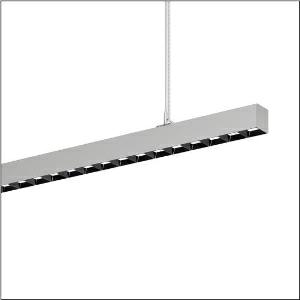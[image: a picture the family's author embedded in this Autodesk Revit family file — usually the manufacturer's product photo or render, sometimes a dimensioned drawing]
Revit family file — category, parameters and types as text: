
# Revit family: silica_r__21_51mx32tat7s_c957
name_source: partatom
category: Lighting Fixtures
units: mm (PartAtom-declared; Revit-internal decimal feet)

## family parameters
Cut with Voids When Loaded = No
Host = Face
Light Source = No
Part Type = Normal
Room Calculation Point = No
Round Connector Dimension = Use Diameter
Shared = No

## types (1)
- --- (1 x LED, 6220 lm, 53.4 W, 6500K)
    Apparent Load = 53 VA
    CIE Flux Codes = 84 99 100 60 100
    Color Rendering = 80
    Color Temperature = 6500K
    Default Elevation = 1800 mm
    Description = Silica® 21, office luminaire, primary light control with darklight reflector, of PMMA, black, CAT 2 (L<= 3000cd/m²), light emission: direct/indirect distribution, primary light characteristic: symmetric, installation type: suspended mounting, LED, rated luminous flux: 6.220lm, luminous efficacy: 111lm/W, light colour: 8tw, colour temperature: 2700..6500K, control gear: ECG DALI, with terminal, 3+2-pole, max. 2.5mm², mains connection: 220..240V, AC, 50/60Hz, rated input power: 56.1W, luminaire housing, of aluminium, metallic grey (RAL 9006), length: 1.204mm, width: 53mm, height: 53mm, protection rating (complete): IP20, insulation class (complete): insulation class I (protective earthing), certification: CE, permissible operating ambient temperature: 0..+35°C, standard: EN 50419, packaging unit: 1 piece
    Height = 53 mm
    Lamp = 1 x LED
    Lamp Light Flux = 6220 lm
    Lamp Power = 53.4 W
    Lamp count = 1
    Length = 1204 mm
    Luminous efficacy = 116 lm/W
    Manufacturer = Siteco
    ModVariant = No
    Model = 51MX32TAT7S
    Mounting Place = Ceiling
    Mounting Type = Pendant
    Number of Poles = 1
    OnlyDefault = Yes
    Power Factor = 1
    Product Name = Silica® 21
    Product group = office luminaire | ceiling pendant
    ProductGroupID = 902
    Protection Class = Protection class I
    Protection Degree = IP 20
    RLX_Detail_Level = 1
    RLX_Emergency_Light_Flux = 0 lm
    RLX_Emergency_Type = 0
    RLX_Emergency_Type_DB = No
    RlxData = <blob elided: 41325 chars, md5=35059f97>
    Socket = socket
    Standby Power = 0 W
    System Light Flux = 6220 lm
    System Power = 53 W
    Type Comments = individual setting
    Type Image = l_1335859.jpg
    URL = http://relux.com
    VarID = @adj_109729
    Voltage = 0 V
    Weight = 0.00 kg
    Width = 53 mm

## geometry (parser evidence)
native form markers: Blend x4, Sweep x12
no freeform markers — native parametric forms only
